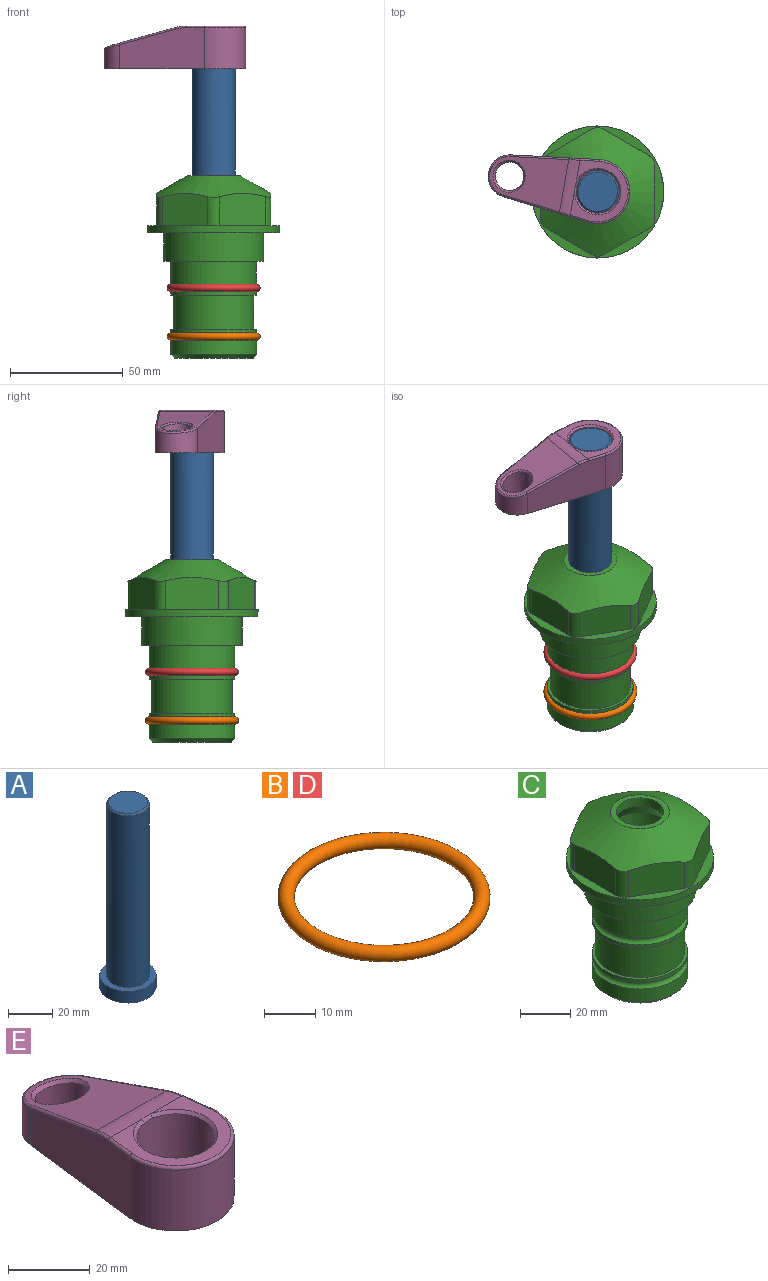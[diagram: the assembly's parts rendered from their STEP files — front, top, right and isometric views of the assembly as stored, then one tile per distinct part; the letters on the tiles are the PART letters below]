
ASSEMBLY  parts=5 mates=4
PART A: 6 faces, bbox 25.4x25.4x101.6 mm
  f0: plane 17.46x17.46mm, normal (0,0,1), area 239.5mm2, adj f5
  f1: plane 25.4x25.4mm, normal (0,0,-1), area 506.7mm2, adj f2
  f2: cylinder r=12.7mm len=25.4mm, axis (0,0,1), area 506.7mm2, adj f1,f3
  f3: plane 25.4x25.4mm, normal (0,0,1), area 221.7mm2, adj f2,f4
  f4: cylinder r=9.53mm len=94.46mm, axis (0,0,1), area 5653mm2, adj f3,f5
  f5: cone r=8.73mm half-angle=45deg, axis (0,0,-1), area 64.4mm2, adj f0,f4
PART B: 1 faces, bbox 44.7x44.7x3.2 mm
  f0: torus R=19.05mm, axis (0,0,1), area 1193.9mm2
PART C: 36 faces, bbox 58.7x58.7x81 mm
  f0: cylinder r=17.78mm len=35.56mm, axis (0,0,1), area 1670.8mm2, adj f23,f24,f31
  f1: cylinder r=19.05mm len=38.1mm, axis (0,0,1), area 1191.9mm2, adj f26,f27,f30
  f2: plane 58.66x58.66mm, normal (0,0,-1), area 1150.6mm2, adj f3,f28
  f3: cylinder r=29.33mm len=58.66mm, axis (0,0,-1), area 585.1mm2, adj f2,f4
  f4: plane 58.66x58.66mm, normal (0,0,1), area 475.9mm2, adj f3,f5,f6,f7,f8,f9,f10,f11
  f5: plane 20.32x14.34mm, normal (-0.5,0.87,0), area 324.4mm2, adj f4,f15,f16,f17
  f6: plane 20.32x14.34mm, normal (0.5,0.87,0), area 324.4mm2, adj f4,f14,f15,f17
  f7: plane 23.48x14.34mm, normal (1,0,0), area 324.4mm2, adj f4,f13,f14,f17
  f8: plane 20.32x14.34mm, normal (0.5,-0.87,0), area 324.4mm2, adj f4,f12,f13,f17
  f9: plane 20.32x14.34mm, normal (-0.5,-0.87,0), area 324.4mm2, adj f4,f11,f12,f17
  f10: plane 23.48x14.34mm, normal (-1,0,0), area 324.4mm2, adj f4,f11,f16,f17
  f11: cylinder r=5.08mm len=12.85mm, axis (0,0,-1), area 67.2mm2, adj f4,f9,f10,f17
  f12: cylinder r=5.08mm len=12.85mm, axis (0,0,-1), area 67.2mm2, adj f4,f8,f9,f17
  f13: cylinder r=5.08mm len=12.85mm, axis (0,0,-1), area 67.2mm2, adj f4,f7,f8,f17
  f14: cylinder r=5.08mm len=12.85mm, axis (0,0,-1), area 67.2mm2, adj f4,f6,f7,f17
  f15: cylinder r=5.08mm len=12.85mm, axis (0,0,-1), area 67.2mm2, adj f4,f5,f6,f17
  f16: cylinder r=5.08mm len=12.85mm, axis (0,0,-1), area 67.2mm2, adj f4,f5,f10,f17
  f17: cone r=11.73mm half-angle=60deg, axis (0,0,-1), area 2071.8mm2, adj f5,f6,f7,f8,f9,f10,f11,f12
  f18: plane 23.46x23.46mm, normal (0,0,1), area 147.4mm2, adj f17,f35
  f19: plane 34.93x34.93mm, normal (0,0,-1), area 958mm2, adj f29
  f20: cylinder r=19.05mm len=38.1mm, axis (0,0,1), area 760.1mm2, adj f21,f29
  f21: torus R=19.05mm, axis (0,0,1), area 565.3mm2, adj f20,f22
  f22: cylinder r=19.05mm len=38.1mm, axis (0,0,1), area 190mm2, adj f21,f23
  f23: plane 38.1x38.1mm, normal (0,0,1), area 146.9mm2, adj f0,f22
  f24: plane 38.1x38.1mm, normal (0,0,-1), area 146.9mm2, adj f0,f25
  f25: cylinder r=19.05mm len=38.1mm, axis (0,0,1), area 190mm2, adj f24,f26
  f26: torus R=19.05mm, axis (0,0,1), area 565.3mm2, adj f1,f25
  f27: plane 44.45x44.45mm, normal (0,0,-1), area 411.7mm2, adj f1,f28
  f28: cylinder r=22.23mm len=44.45mm, axis (0,0,1), area 1773.5mm2, adj f2,f27
  f29: cone r=19.05mm half-angle=45deg, axis (0,0,1), area 257.5mm2, adj f19,f20
  f30: cylinder r=3.17mm len=6.75mm, axis (-1,0,0), area 128mm2, adj f1,f33
  f31: cylinder r=3.17mm len=6.35mm, axis (-1,0,0), area 102.5mm2, adj f0,f33
  f32: plane 25.4x25.4mm, normal (0,0,1), area 506.7mm2, adj f33
  f33: cylinder r=12.7mm len=66.42mm, axis (0,0,-1), area 5236.2mm2, adj f30,f31,f32,f34
  f34: cone r=9.53mm half-angle=30deg, axis (0,0,-1), area 443.4mm2, adj f33,f35
  f35: cylinder r=9.53mm len=19.05mm, axis (0,0,-1), area 240.9mm2, adj f18,f34
PART D: same geometry as B
PART E: 31 faces, bbox 31.7x65.5x19.8 mm
  f0: plane 39.12x18.26mm, normal (0.99,0.12,0), area 612.2mm2, adj f1,f4,f7,f11,f13,f15
  f1: cylinder r=9.53mm len=18.91mm, axis (0,0,-1), area 296.1mm2, adj f0,f2,f7,f17
  f2: plane 39.12x18.26mm, normal (-0.99,0.12,0), area 612.2mm2, adj f1,f4,f7,f12,f14,f16
  f3: cylinder r=6.35mm len=12.7mm, axis (0,0,-1), area 362.4mm2, adj f7,f18
  f4: cylinder r=14.29mm len=28.58mm, axis (0,0,-1), area 882.2mm2, adj f0,f2,f7,f10
  f5: cylinder r=9.53mm len=19.05mm, axis (0,0,-1), area 1092.6mm2, adj f7,f19,f20
  f6: plane 26.99x23.69mm, normal (0,0,1), area 216.2mm2, adj f9,f10,f11,f12,f19
  f7: plane 63.5x28.58mm, normal (0,0,-1), area 661.8mm2, adj f0,f1,f2,f3,f4,f5,f22,f23
  f8: plane 33.52x23.6mm, normal (0,0.26,0.97), area 486mm2, adj f9,f15,f16,f17,f18
  f9: cylinder r=19.05mm len=24.72mm, axis (1,0,0), area 120.4mm2, adj f6,f8,f13,f14,f20
  f10: torus R=13.49mm, axis (0,0,1), area 59mm2, adj f4,f6,f11,f12
  f11: cylinder r=0.79mm len=8.67mm, axis (0.12,-0.99,0), area 10.8mm2, adj f0,f6,f10,f13
  f12: cylinder r=0.79mm len=8.67mm, axis (0.12,0.99,0), area 10.8mm2, adj f2,f6,f10,f14
  f13: bspline ~4.95x1.42mm, area 6.1mm2, adj f0,f9,f11,f15
  f14: bspline ~4.95x1.42mm, area 6.1mm2, adj f2,f9,f12,f16
  f15: cylinder r=0.79mm len=25.95mm, axis (0.12,-0.96,0.26), area 32.9mm2, adj f0,f8,f13,f17
  f16: cylinder r=0.79mm len=25.95mm, axis (0.12,0.96,-0.26), area 32.9mm2, adj f2,f8,f14,f17
  f17: bspline ~18.91x8.38mm, area 30mm2, adj f1,f8,f15,f16
  f18: bspline ~14.29x14.29mm, area 48.3mm2, adj f3,f8
  f19: cone r=9.53mm half-angle=45deg, axis (0,0,1), area 66.5mm2, adj f5,f6,f20
  f20: bspline ~3.22x0.96mm, area 3.5mm2, adj f5,f9,f19
  f21: plane 2.75x2.72mm, normal (0,0,-1), area 2.9mm2, adj f23,f25,f28
  f22: plane 23.05x15.88mm, normal (-0.99,-0.12,0), area 323.6mm2, adj f7,f25,f26,f27,f28,f29
  f23: plane 23.05x15.88mm, normal (0.99,-0.12,0), area 323.6mm2, adj f7,f21,f25,f27,f28,f30
  f24: cylinder r=9.53mm len=10.69mm, axis (0,0,-1), area 114.7mm2, adj f7,f27,f29,f30
  f25: cylinder r=12.7mm len=20.59mm, axis (0,0,-1), area 381.1mm2, adj f7,f21,f22,f23,f26,f28
  f26: plane 2.75x2.72mm, normal (0,0,-1), area 2.9mm2, adj f22,f25,f28
  f27: plane 19.72x18.37mm, normal (0,-0.26,-0.97), area 291.8mm2, adj f22,f23,f24,f28,f29,f30
  f28: cylinder r=15.88mm len=19.92mm, axis (1,0,0), area 54.8mm2, adj f21,f22,f23,f25,f26,f27
  f29: cylinder r=1.59mm len=11mm, axis (0,0,-1), area 34.7mm2, adj f7,f22,f24,f27
  f30: cylinder r=1.59mm len=11mm, axis (0,0,-1), area 34.7mm2, adj f7,f23,f24,f27
PLACE A rot(axis=(0,0,1),80.1deg) t=(0,0,27.55)mm
PLACE B t=(0,0,-21.59)mm
PLACE C at identity fixed
PLACE D at identity
PLACE E rot(axis=(0,0,1),80.1deg) t=(0,0,28.35)mm
MATE fastened C.f0 <-> D.f0  axis (0,0,1) through (0,0,-24.51)mm
MATE cylindrical C.f0 <-> A.f2  axis (0,0,1) through (0,0,-50.55)mm
MATE fastened B.f0 <-> C.f0  axis (0,0,1) through (0,0,-46.1)mm
MATE fastened A.f2 <-> E.f4  axis (0,0,1) through (0,0,91.05)mm
